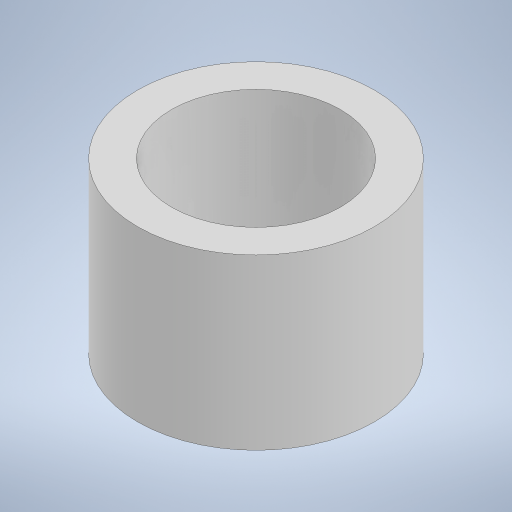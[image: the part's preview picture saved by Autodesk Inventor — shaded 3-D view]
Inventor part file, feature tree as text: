
AUTODESK INVENTOR PART (.ipt)
format: ipt  version: 2023 (Build 270158000, 158)  size: 187,392 bytes
history: native  units: mm
features: extrude x1, sketch x1
ambient origin geometry x8: Origin, YZ Plane, XZ Plane, XY Plane, X Axis, Y Axis, Z Axis, Center Point
bodies: Solid1 (feature_tree)
feature tree (2):
  extrude  "Extrusion1"  Depth=10.0mm
  sketch  "Sketch1"  dims[d0=10.0mm d2=14.0mm d3=10.0mm d4=0.0mm]
